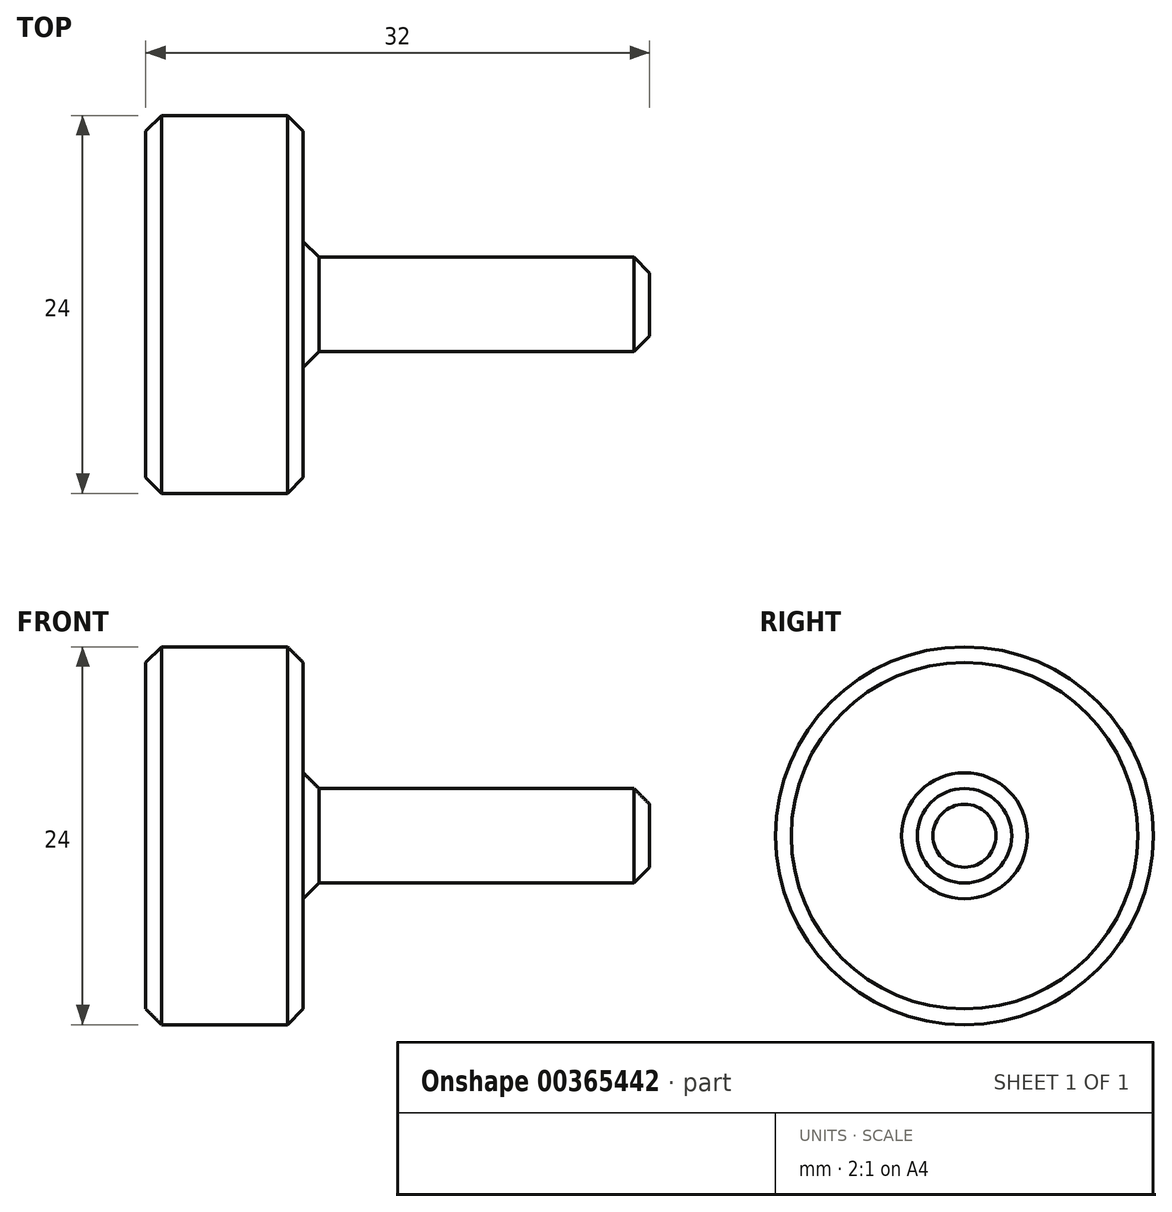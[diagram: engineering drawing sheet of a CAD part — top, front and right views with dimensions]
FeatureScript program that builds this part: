
annotation { "Feature Type Name" : "Feature", "Feature Type Description" : "" }
export const myFeature = defineFeature(function(context is Context, id is Id, definition is map)
    precondition{}
    {
        {
            var Q0;
            Q0=qCreatedBy(makeId("Front.planeOp"),FACE);
            var sketch = newSketch(context, id + "F0", { "sketchPlane" : qUnion([Q0])});
            skLineSegment(sketch, "E0", {"start": v(16.76, 0) * mm, "end": v(16.76, 3) * mm});
            skLineSegment(sketch, "E1", {"start": v(16.76, 3) * mm, "end": v(-5.24, 3) * mm});
            skLineSegment(sketch, "E2", {"start": v(-5.24, 3) * mm, "end": v(-5.24, 12) * mm});
            skLineSegment(sketch, "E3", {"start": v(-5.24, 12) * mm, "end": v(-15.24, 12) * mm});
            skLineSegment(sketch, "E4", {"start": v(-15.24, 12) * mm, "end": v(-15.24, 0) * mm});
            skLineSegment(sketch, "E5", {"start": v(-15.24, 0) * mm, "end": v(16.76, 0) * mm});
            skSolve(sketch);
        }
        {
            var Q0;
            Q0=makeQuery(id+"F0.imprint","IMPRINT",FACE,{"disambiguationData":[TD([[makeQuery(id+"F0.imprint","IMPRINT",EDGE,{"derivedFrom":sQuery(id+"F0.wireOp",EDGE,"E0")}),1.0]])]});
            var Q1;
            Q1=sQuery(id+"F0.wireOp",EDGE,"E5");
            revolve(context, id + "F1", {"entities" : qUnion([Q0]), "axis" : qUnion([Q1]), "revolveType" : RevolveType.FULL});
        }
        {
            var Q0;
            Q0=makeQuery(id+"F1.opRevolve","SWEPT_EDGE",EDGE,{"disambiguationData":[OSD([sQuery(id+"F0.wireOp",EDGE,"E2"),sQuery(id+"F0.wireOp",EDGE,"E3")])]});
            var Q1;
            Q1=makeQuery(id+"F1.opRevolve","SWEPT_EDGE",EDGE,{"disambiguationData":[OSD([sQuery(id+"F0.wireOp",EDGE,"E3"),sQuery(id+"F0.wireOp",EDGE,"E4")])]});
            var Q2;
            Q2=makeQuery(id+"F1.opRevolve","SWEPT_FACE",FACE,{"disambiguationData":[OSD([sQuery(id+"F0.wireOp",EDGE,"E2")])]});
            var Q3;
            Q3=makeQuery(id+"F1.opRevolve","SWEPT_EDGE",EDGE,{"disambiguationData":[OSD([sQuery(id+"F0.wireOp",EDGE,"E0"),sQuery(id+"F0.wireOp",EDGE,"E1")])]});
            chamfer(context, id + "F2", {"entities" : qUnion([Q0, Q1, Q2, Q3]), "width" : 1 * mm, "tangentPropagation" : true});
        }
    });
